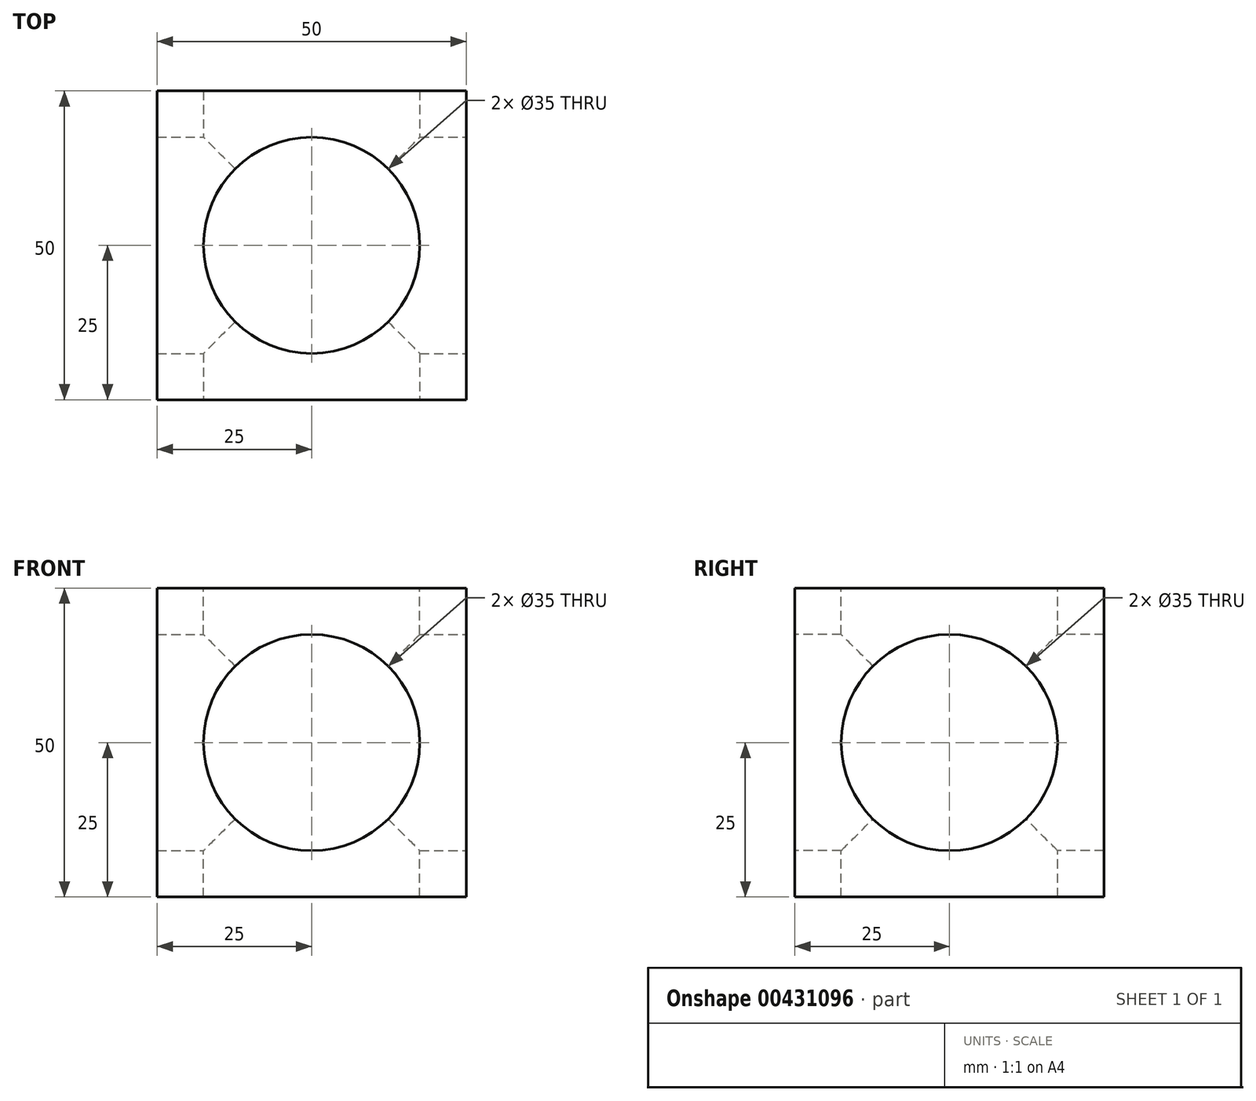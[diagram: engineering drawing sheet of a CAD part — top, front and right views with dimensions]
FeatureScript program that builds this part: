
annotation { "Feature Type Name" : "Feature", "Feature Type Description" : "" }
export const myFeature = defineFeature(function(context is Context, id is Id, definition is map)
    precondition{}
    {
        {
            var Q0;
            Q0=qCreatedBy(makeId("Front.planeOp"),FACE);
            var sketch = newSketch(context, id + "F0", { "sketchPlane" : qUnion([Q0])});
            skLineSegment(sketch, "E0.bottom", {"start": v(25, -25) * mm, "end": v(-25, -25) * mm});
            skLineSegment(sketch, "E0.top", {"start": v(25, 25) * mm, "end": v(-25, 25) * mm});
            skLineSegment(sketch, "E0.left", {"start": v(25, -25) * mm, "end": v(25, 25) * mm});
            skLineSegment(sketch, "E0.right", {"start": v(-25, -25) * mm, "end": v(-25, 25) * mm});
            skPoint(sketch, "E0.middle", {"position": v(0, 0) * mm});
            skSolve(sketch);
        }
        {
            var Q0;
            Q0 = qSketchRegion(id + "F0", true);
            extrude(context, id + "F1", {"entities" : qUnion([Q0]), "depth" : 50 * mm});
        }
        {
            var Q0;
            Q0=makeQuery(id+"F1.opExtrude","CAP_FACE",FACE,{"disambiguationData":[OSD([sQuery(id+"F0.wireOp",EDGE,"E0.bottom"),sQuery(id+"F0.wireOp",EDGE,"E0.top"),sQuery(id+"F0.wireOp",EDGE,"E0.left"),sQuery(id+"F0.wireOp",EDGE,"E0.right")])],"isStart":false});
            var sketch = newSketch(context, id + "F2", { "sketchPlane" : qUnion([Q0])});
            skCircle(sketch, "E1", {"center": v(0, 0) * mm, "radius": 17.5 * mm});
            skSolve(sketch);
        }
        {
            var Q0;
            Q0 = qSketchRegion(id + "F2", true);
            extrude(context, id + "F3", {"entities" : qUnion([Q0]), "operationType" : NewBodyOperationType.REMOVE, "endBound" : BoundingType.THROUGH_ALL, "oppositeDirection" : true, "depth" : 25 * mm});
        }
        {
            var Q0;
            Q0=makeQuery(id+"F1.opExtrude","SWEPT_FACE",FACE,{"disambiguationData":[OSD([sQuery(id+"F0.wireOp",EDGE,"E0.top")])]});
            var sketch = newSketch(context, id + "F4", { "sketchPlane" : qUnion([Q0])});
            skCircle(sketch, "E2", {"center": v(0, -25) * mm, "radius": 17.5 * mm});
            skPoint(sketch, "E2.centerSnap0", {"position": v(0, -50) * mm});
            skSolve(sketch);
        }
        {
            var Q0;
            Q0 = qSketchRegion(id + "F4", true);
            extrude(context, id + "F5", {"entities" : qUnion([Q0]), "operationType" : NewBodyOperationType.REMOVE, "endBound" : BoundingType.THROUGH_ALL, "oppositeDirection" : true, "depth" : 25 * mm});
        }
        {
            var Q0;
            Q0=makeQuery(id+"F1.opExtrude","SWEPT_FACE",FACE,{"disambiguationData":[OSD([sQuery(id+"F0.wireOp",EDGE,"E0.left")])]});
            var sketch = newSketch(context, id + "F6", { "sketchPlane" : qUnion([Q0])});
            skCircle(sketch, "E3", {"center": v(-25, 0) * mm, "radius": 17.5 * mm});
            skLineSegment(sketch, "E4", {"start": v(-25, 25) * mm, "end": v(-25, -25) * mm, "construction": true});
            skSolve(sketch);
        }
        {
            var Q0;
            Q0 = qSketchRegion(id + "F6", true);
            extrude(context, id + "F7", {"entities" : qUnion([Q0]), "operationType" : NewBodyOperationType.REMOVE, "endBound" : BoundingType.THROUGH_ALL, "oppositeDirection" : true, "depth" : 25 * mm});
        }
    });
